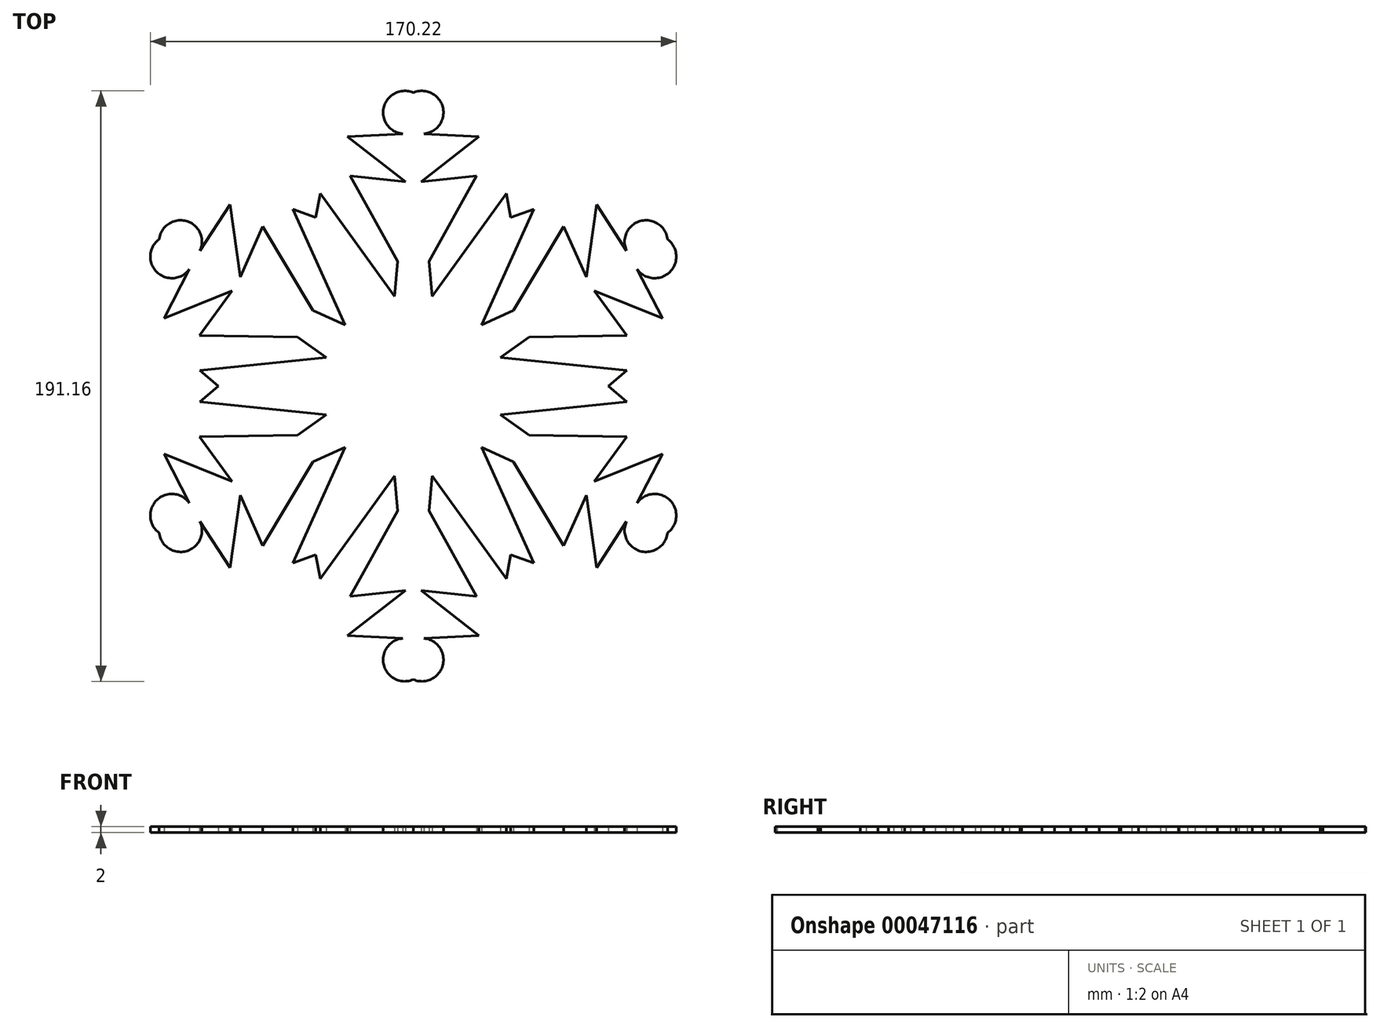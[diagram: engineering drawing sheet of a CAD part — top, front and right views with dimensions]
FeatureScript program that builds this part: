
annotation { "Feature Type Name" : "Feature", "Feature Type Description" : "" }
export const myFeature = defineFeature(function(context is Context, id is Id, definition is map)
    precondition{}
    {
        {
            var Q0;
            Q0=qCreatedBy(makeId("Top.planeOp"),FACE);
            var sketch = newSketch(context, id + "F0", { "sketchPlane" : qUnion([Q0])});
            skLineSegment(sketch, "E0", {"start": v(0, 0) * mm, "end": v(0, 95) * mm, "construction": true});
            skArc(sketch, "E1", {"start": v(0, 82.23) * mm, "mid": v(9.76, 88.62) * mm, "end": v(0, 95) * mm});
            skLineSegment(sketch, "E2", {"start": v(3.43, 81.68) * mm, "end": v(21.28, 80.8) * mm});
            skLineSegment(sketch, "E3", {"start": v(21.28, 80.8) * mm, "end": v(2.57, 66.18) * mm});
            skLineSegment(sketch, "E4", {"start": v(2.57, 66.18) * mm, "end": v(20.43, 68.04) * mm});
            skLineSegment(sketch, "E5", {"start": v(20.43, 68.04) * mm, "end": v(5.03, 40.38) * mm});
            skLineSegment(sketch, "E6", {"start": v(5.03, 40.38) * mm, "end": v(6.09, 29.09) * mm});
            skLineSegment(sketch, "E7", {"start": v(6.09, 29.09) * mm, "end": v(30.1, 62.37) * mm});
            skLineSegment(sketch, "E8", {"start": v(30.1, 62.37) * mm, "end": v(32.23, 51.15) * mm});
            skLineSegment(sketch, "E9", {"start": v(32.23, 51.15) * mm, "end": v(5.81, 0) * mm});
            skLineSegment(sketch, "E10", {"start": v(5.81, 0) * mm, "end": v(0, 0) * mm});
            skLineSegment(sketch, "E11", {"start": v(0, 95) * mm, "end": v(0, 0) * mm});
            skSolve(sketch);
        }
        {
            var Q0;
            Q0 = qSketchRegion(id + "F0", true);
            extrude(context, id + "F1", {"entities" : qUnion([Q0]), "depth" : 2 * mm});
        }
        {
            var Q0;
            Q0=makeQuery(id+"F1.opExtrude","SWEPT_BODY",BODY,{"disambiguationData":[OSD([sQuery(id+"F0.wireOp",EDGE,"E1"),sQuery(id+"F0.wireOp",EDGE,"E2"),sQuery(id+"F0.wireOp",EDGE,"E3"),sQuery(id+"F0.wireOp",EDGE,"E4"),sQuery(id+"F0.wireOp",EDGE,"E5"),sQuery(id+"F0.wireOp",EDGE,"E6"),sQuery(id+"F0.wireOp",EDGE,"E7"),sQuery(id+"F0.wireOp",EDGE,"E8"),sQuery(id+"F0.wireOp",EDGE,"E9"),sQuery(id+"F0.wireOp",EDGE,"E10"),sQuery(id+"F0.wireOp",EDGE,"E11")])]});
            var Q1;
            Q1=qCreatedBy(makeId("Right.planeOp"),FACE);
            mirror(context, id + "F2", {"operationType" : NewBodyOperationType.ADD, "entities" : qUnion([Q0]), "mirrorPlane" : qUnion([Q1])});
        }
        {
            var Q0;
            Q0=qCreatedBy(makeId("Front.planeOp"),FACE);
            var sketch = newSketch(context, id + "F3", { "sketchPlane" : qUnion([Q0])});
            skLineSegment(sketch, "E12", {"start": v(0, 0) * mm, "end": v(0, 8.23) * mm});
            skSolve(sketch);
        }
        {
            var Q0;
            Q0=makeQuery(id+"F1.opExtrude","SWEPT_BODY",BODY,{"disambiguationData":[OSD([sQuery(id+"F0.wireOp",EDGE,"E1"),sQuery(id+"F0.wireOp",EDGE,"E2"),sQuery(id+"F0.wireOp",EDGE,"E3"),sQuery(id+"F0.wireOp",EDGE,"E4"),sQuery(id+"F0.wireOp",EDGE,"E5"),sQuery(id+"F0.wireOp",EDGE,"E6"),sQuery(id+"F0.wireOp",EDGE,"E7"),sQuery(id+"F0.wireOp",EDGE,"E8"),sQuery(id+"F0.wireOp",EDGE,"E9"),sQuery(id+"F0.wireOp",EDGE,"E10"),sQuery(id+"F0.wireOp",EDGE,"E11")])]});
            var Q1;
            Q1=sQuery(id+"F3.wireOp",EDGE,"E12");
            circularPattern(context, id + "F4", {"operationType" : NewBodyOperationType.ADD, "entities" : qUnion([Q0]), "axis" : qUnion([Q1]), "angle" : 60 * degree, "instanceCount" : round(6)});
        }
    });
